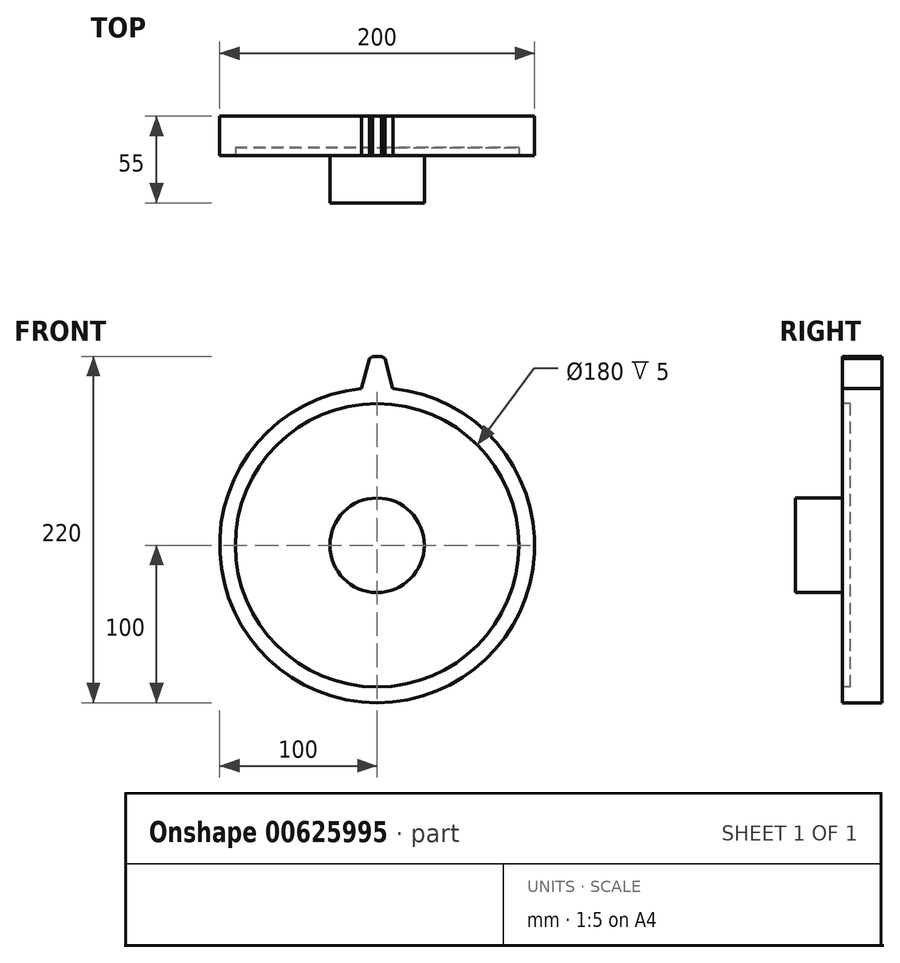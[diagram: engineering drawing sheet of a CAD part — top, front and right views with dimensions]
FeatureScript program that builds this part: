
annotation { "Feature Type Name" : "Feature", "Feature Type Description" : "" }
export const myFeature = defineFeature(function(context is Context, id is Id, definition is map)
    precondition{}
    {
        {
            var Q0;
            Q0=qCreatedBy(makeId("Front.planeOp"),FACE);
            var sketch = newSketch(context, id + "F0", { "sketchPlane" : qUnion([Q0])});
            skCircle(sketch, "E0", {"center": v(0, 0) * mm, "radius": 100 * mm});
            skSolve(sketch);
        }
        {
            var Q0;
            Q0=makeQuery(id+"F0.imprint","IMPRINT",FACE,{"disambiguationData":[TD([[makeQuery(id+"F0.imprint","IMPRINT",EDGE,{"derivedFrom":sQuery(id+"F0.wireOp",EDGE,"E0")}),1.0]])]});
            extrude(context, id + "F1", {"entities" : qUnion([Q0]), "depth" : 25 * mm, "offsetDistance" : 25 * mm});
        }
        {
            var Q0;
            Q0=makeQuery(id+"F1.opExtrude","CAP_FACE",FACE,{"disambiguationData":[OSD([sQuery(id+"F0.wireOp",EDGE,"E0")])],"isStart":false});
            var sketch = newSketch(context, id + "F2", { "sketchPlane" : qUnion([Q0])});
            skLineSegment(sketch, "E1", {"start": v(-10, 99.5) * mm, "end": v(10, 99.5) * mm});
            skLineSegment(sketch, "E2", {"start": v(10, 99.5) * mm, "end": v(4.5, 120) * mm});
            skLineSegment(sketch, "E3", {"start": v(4.5, 120) * mm, "end": v(-4.5, 120) * mm});
            skLineSegment(sketch, "E4", {"start": v(-4.5, 120) * mm, "end": v(-10, 99.5) * mm});
            skSolve(sketch);
        }
        {
            var Q0;
            {var subQ0=sQuery(id+"F2.wireOp",EDGE,"E1");Q0=makeQuery(id+"F2.imprint","IMPRINT",FACE,{"disambiguationData":[TD([[makeQuery(id+"F2.imprint","IMPRINT",EDGE,{"derivedFrom":subQ0}),-1.0]])]});}
            var Q1;
            {var subQ0=sQuery(id+"F2.wireOp",EDGE,"E2");Q1=makeQuery(id+"F2.imprint","IMPRINT",FACE,{"disambiguationData":[TD([[makeQuery(id+"F2.imprint","IMPRINT",EDGE,{"derivedFrom":subQ0}),1.0]])]});}
            extrude(context, id + "F3", {"entities" : qUnion([Q0, Q1]), "operationType" : NewBodyOperationType.ADD, "oppositeDirection" : true, "depth" : 25 * mm, "offsetDistance" : 25 * mm});
        }
        {
            var Q0;
            Q0=makeQuery(id+"F3.opExtrude","SWEPT_EDGE",EDGE,{"disambiguationData":[OSD([sQuery(id+"F2.wireOp",EDGE,"E3"),sQuery(id+"F2.wireOp",EDGE,"E4")])]});
            var Q1;
            Q1=makeQuery(id+"F3.opExtrude","SWEPT_EDGE",EDGE,{"disambiguationData":[OSD([sQuery(id+"F2.wireOp",EDGE,"E2"),sQuery(id+"F2.wireOp",EDGE,"E3")])]});
            chamfer(context, id + "F4", {"entities" : qUnion([Q0, Q1]), "width" : 2 * mm, "tangentPropagation" : true});
        }
        {
            var Q0;
            Q0=makeQuery(id+"F3.opExtrude","SWEPT_EDGE",EDGE,{"disambiguationData":[OSD([sQuery(id+"F0.wireOp",EDGE,"E0"),sQuery(id+"F2.wireOp",EDGE,"E1"),sQuery(id+"F2.wireOp",EDGE,"E2")]),OD(1.0)]});
            var Q1;
            Q1=makeQuery(id+"F3.opExtrude","SWEPT_EDGE",EDGE,{"disambiguationData":[OSD([sQuery(id+"F0.wireOp",EDGE,"E0"),sQuery(id+"F2.wireOp",EDGE,"E1"),sQuery(id+"F2.wireOp",EDGE,"E4")]),OD(1.0)]});
            fillet(context, id + "F5", {"entities" : qUnion([Q0, Q1]), "radius" : 5 * mm, "tangentPropagation" : true, "allowEdgeOverflow" : false});
        }
        {
            var Q0;
            {var subQ0=sQuery(id+"F2.wireOp",EDGE,"E1");Q0=makeQuery(id+"F2.imprint","IMPRINT",FACE,{"disambiguationData":[TD([[makeQuery(id+"F2.imprint","IMPRINT",EDGE,{"derivedFrom":subQ0}),-1.0]])]});}
            var sketch = newSketch(context, id + "F6", { "sketchPlane" : qUnion([Q0])});
            skCircle(sketch, "E5", {"center": v(0, 0) * mm, "radius": 90 * mm});
            skSolve(sketch);
        }
        {
            var Q0;
            Q0 = qSketchRegion(id + "F6", true);
            extrude(context, id + "F7", {"entities" : qUnion([Q0]), "operationType" : NewBodyOperationType.REMOVE, "oppositeDirection" : true, "depth" : 5 * mm, "offsetDistance" : 25 * mm});
        }
        {
            var Q0;
            {var subQ0=sQuery(id+"F2.wireOp",EDGE,"E1");Q0=makeQuery(id+"F2.imprint","IMPRINT",FACE,{"disambiguationData":[TD([[makeQuery(id+"F2.imprint","IMPRINT",EDGE,{"derivedFrom":subQ0}),-1.0]])]});}
            var sketch = newSketch(context, id + "F8", { "sketchPlane" : qUnion([Q0])});
            skCircle(sketch, "E6", {"center": v(0, 0) * mm, "radius": 30 * mm});
            skSolve(sketch);
        }
        {
            var Q0;
            Q0 = qSketchRegion(id + "F8", true);
            extrude(context, id + "F9", {"entities" : qUnion([Q0]), "operationType" : NewBodyOperationType.ADD, "depth" : 30 * mm, "offsetDistance" : 25 * mm});
        }
    });
